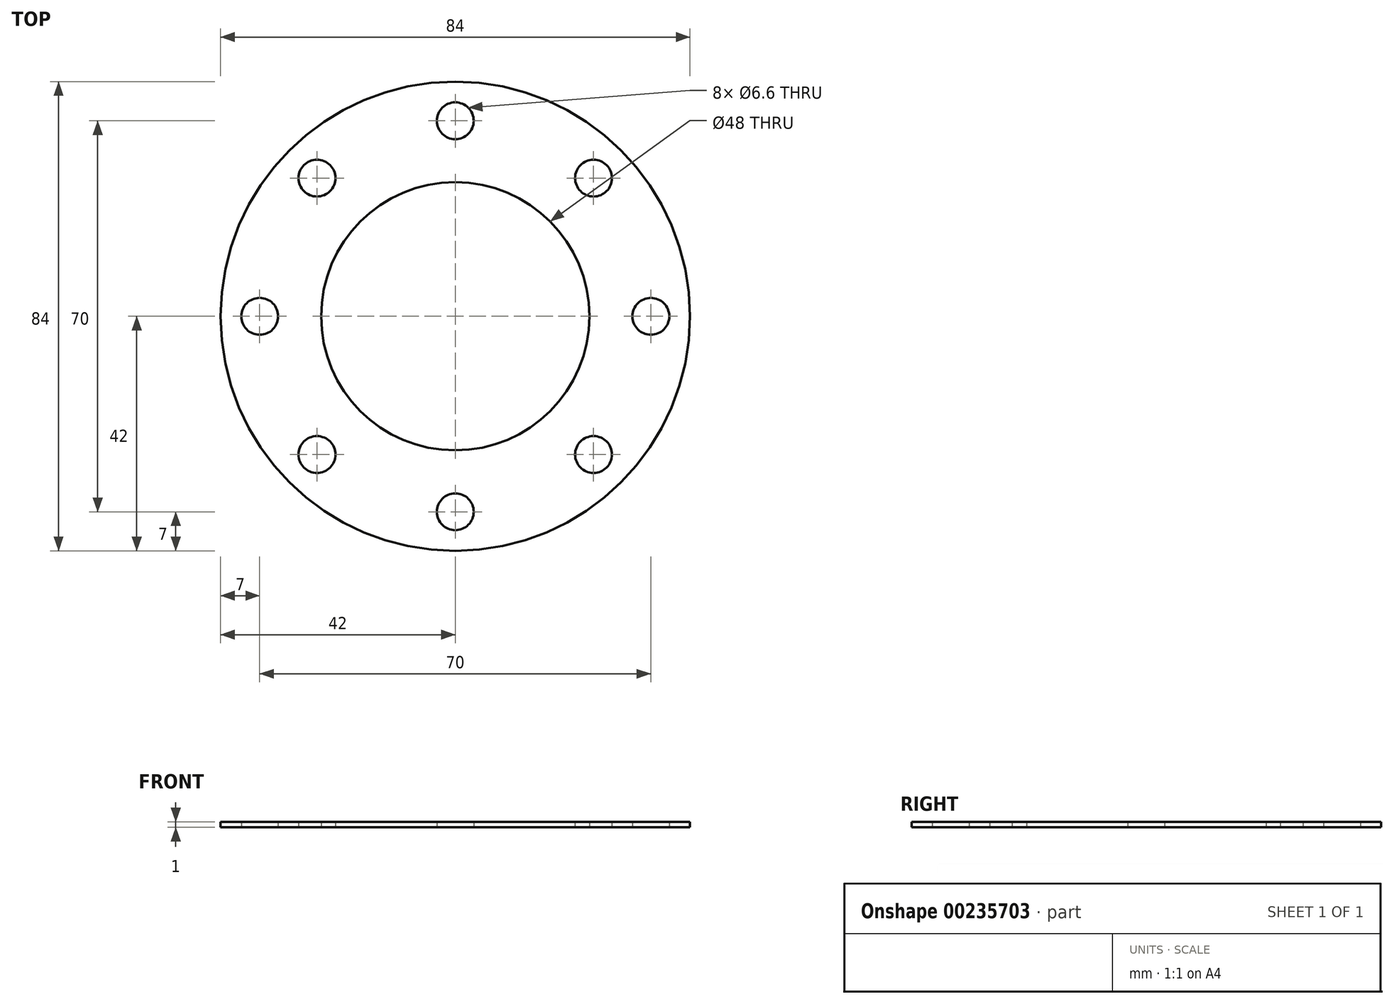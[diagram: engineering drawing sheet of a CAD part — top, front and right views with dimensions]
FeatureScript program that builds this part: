
annotation { "Feature Type Name" : "Feature", "Feature Type Description" : "" }
export const myFeature = defineFeature(function(context is Context, id is Id, definition is map)
    precondition{}
    {
        {
            var Q0;
            Q0=qCreatedBy(makeId("Top.planeOp"),FACE);
            var sketch = newSketch(context, id + "F0", { "sketchPlane" : qUnion([Q0])});
            skCircle(sketch, "E0", {"center": v(0, 0) * mm, "radius": 42 * mm});
            skCircle(sketch, "E1", {"center": v(0, 0) * mm, "radius": 24 * mm});
            skLineSegment(sketch, "E2", {"start": v(0, 0) * mm, "end": v(0, 35) * mm, "construction": true});
            skCircle(sketch, "E3", {"center": v(0, 0) * mm, "radius": 35 * mm, "construction": true});
            skLineSegment(sketch, "E4", {"start": v(0, 0) * mm, "end": v(0, -35) * mm, "construction": true});
            skLineSegment(sketch, "E5", {"start": v(0, 0) * mm, "end": v(35, 0) * mm, "construction": true});
            skLineSegment(sketch, "E6", {"start": v(0, 0) * mm, "end": v(-35, 0) * mm, "construction": true});
            skLineSegment(sketch, "E7", {"start": v(0, 0) * mm, "end": v(24.75, -24.75) * mm, "construction": true});
            skLineSegment(sketch, "E8", {"start": v(0, 0) * mm, "end": v(-24.75, -24.75) * mm, "construction": true});
            skLineSegment(sketch, "E9", {"start": v(0, 0) * mm, "end": v(-24.75, 24.75) * mm, "construction": true});
            skLineSegment(sketch, "E10", {"start": v(0, 0) * mm, "end": v(24.75, 24.75) * mm, "construction": true});
            skPoint(sketch, "E11.orphan", {"position": v(0, 42) * mm});
            skSolve(sketch);
        }
        {
            var Q0;
            Q0=makeQuery(id+"F0.imprint","IMPRINT",FACE,{"disambiguationData":[TD([[makeQuery(id+"F0.imprint","IMPRINT",EDGE,{"derivedFrom":sQuery(id+"F0.wireOp",EDGE,"E0")}),1.0]])]});
            var Q1;
            {var subQ0=sQuery(id+"F0.wireOp",EDGE,"8358ee84-de08-4119-9a5a-cfbe7e3d5f32.7.0");var subQ1=sQuery(id+"F0.wireOp",EDGE,"E1");var subQ2=makeQuery(id+"F0.imprint","INTERSECT",VERTEX,{"derivedFrom":[subQ1,subQ0]});Q1=makeQuery(id+"F0.imprint","IMPRINT",FACE,{"disambiguationData":[TD([[makeQuery(id+"F0.imprint","IMPRINT",EDGE,{"disambiguationData":[TD([[subQ2,1.0]])],"derivedFrom":subQ1}),-1.0]])]});}
            var Q2;
            {var subQ0=sQuery(id+"F0.wireOp",EDGE,"8358ee84-de08-4119-9a5a-cfbe7e3d5f32.7.0");var subQ1=sQuery(id+"F0.wireOp",EDGE,"E1");var subQ2=makeQuery(id+"F0.imprint","INTERSECT",VERTEX,{"derivedFrom":[subQ1,subQ0]});Q2=makeQuery(id+"F0.imprint","IMPRINT",FACE,{"disambiguationData":[TD([[makeQuery(id+"F0.imprint","IMPRINT",EDGE,{"disambiguationData":[TD([[subQ2,-1.0]])],"derivedFrom":subQ1}),-1.0]])]});}
            var Q3;
            {var subQ0=sQuery(id+"F0.wireOp",EDGE,"E2");var subQ1=sQuery(id+"F0.wireOp",EDGE,"E1");var subQ2=makeQuery(id+"F0.imprint","INTERSECT",VERTEX,{"derivedFrom":[subQ1,subQ0]});Q3=makeQuery(id+"F0.imprint","IMPRINT",FACE,{"disambiguationData":[TD([[makeQuery(id+"F0.imprint","IMPRINT",EDGE,{"disambiguationData":[TD([[subQ2,-1.0]])],"derivedFrom":subQ1}),-1.0]])]});}
            var Q4;
            {var subQ0=sQuery(id+"F0.wireOp",EDGE,"8358ee84-de08-4119-9a5a-cfbe7e3d5f32.4.0");var subQ1=sQuery(id+"F0.wireOp",EDGE,"E1");var subQ2=makeQuery(id+"F0.imprint","INTERSECT",VERTEX,{"derivedFrom":[subQ1,subQ0]});Q4=makeQuery(id+"F0.imprint","IMPRINT",FACE,{"disambiguationData":[TD([[makeQuery(id+"F0.imprint","IMPRINT",EDGE,{"disambiguationData":[TD([[subQ2,-1.0]])],"derivedFrom":subQ1}),-1.0]])]});}
            var Q5;
            {var subQ0=sQuery(id+"F0.wireOp",EDGE,"8358ee84-de08-4119-9a5a-cfbe7e3d5f32.6.0");var subQ1=sQuery(id+"F0.wireOp",EDGE,"E1");var subQ2=makeQuery(id+"F0.imprint","INTERSECT",VERTEX,{"derivedFrom":[subQ1,subQ0]});Q5=makeQuery(id+"F0.imprint","IMPRINT",FACE,{"disambiguationData":[TD([[makeQuery(id+"F0.imprint","IMPRINT",EDGE,{"disambiguationData":[TD([[subQ2,1.0]])],"derivedFrom":subQ1}),-1.0]])]});}
            var Q6;
            {var subQ0=sQuery(id+"F0.wireOp",EDGE,"8358ee84-de08-4119-9a5a-cfbe7e3d5f32.3.0");var subQ1=sQuery(id+"F0.wireOp",EDGE,"E1");var subQ2=makeQuery(id+"F0.imprint","INTERSECT",VERTEX,{"derivedFrom":[subQ1,subQ0]});Q6=makeQuery(id+"F0.imprint","IMPRINT",FACE,{"disambiguationData":[TD([[makeQuery(id+"F0.imprint","IMPRINT",EDGE,{"disambiguationData":[TD([[subQ2,-1.0]])],"derivedFrom":subQ1}),-1.0]])]});}
            var Q7;
            {var subQ0=sQuery(id+"F0.wireOp",EDGE,"8358ee84-de08-4119-9a5a-cfbe7e3d5f32.2.0");var subQ1=sQuery(id+"F0.wireOp",EDGE,"E1");var subQ2=makeQuery(id+"F0.imprint","INTERSECT",VERTEX,{"derivedFrom":[subQ1,subQ0]});Q7=makeQuery(id+"F0.imprint","IMPRINT",FACE,{"disambiguationData":[TD([[makeQuery(id+"F0.imprint","IMPRINT",EDGE,{"disambiguationData":[TD([[subQ2,-1.0]])],"derivedFrom":subQ1}),-1.0]])]});}
            var Q8;
            {var subQ0=sQuery(id+"F0.wireOp",EDGE,"8358ee84-de08-4119-9a5a-cfbe7e3d5f32.1.0");var subQ1=sQuery(id+"F0.wireOp",EDGE,"E1");var subQ2=makeQuery(id+"F0.imprint","INTERSECT",VERTEX,{"derivedFrom":[subQ1,subQ0]});Q8=makeQuery(id+"F0.imprint","IMPRINT",FACE,{"disambiguationData":[TD([[makeQuery(id+"F0.imprint","IMPRINT",EDGE,{"disambiguationData":[TD([[subQ2,-1.0]])],"derivedFrom":subQ1}),-1.0]])]});}
            extrude(context, id + "F1", {"entities" : qUnion([Q0, Q1, Q2, Q3, Q4, Q5, Q6, Q7, Q8]), "depth" : 1 * mm});
        }
        {
            var Q0;
            Q0=sQuery(id+"F0.wireOp",VERTEX,"E8.end");
            var Q1;
            Q1=sQuery(id+"F0.wireOp",VERTEX,"E4.end");
            var Q2;
            Q2=sQuery(id+"F0.wireOp",VERTEX,"E7.end");
            var Q3;
            Q3=sQuery(id+"F0.wireOp",VERTEX,"E5.end");
            var Q4;
            Q4=sQuery(id+"F0.wireOp",VERTEX,"E10.end");
            var Q5;
            Q5=sQuery(id+"F0.wireOp",VERTEX,"E2.end");
            var Q6;
            Q6=sQuery(id+"F0.wireOp",VERTEX,"E9.end");
            var Q7;
            Q7=sQuery(id+"F0.wireOp",VERTEX,"E6.end");
            var Q8;
            Q8=makeQuery(id+"F1.opExtrude","SWEPT_BODY",BODY,{"disambiguationData":[OSD([sQuery(id+"F0.wireOp",EDGE,"E0"),sQuery(id+"F0.wireOp",EDGE,"E1")])]});
            hole(context, id + "F2", {"style" : HoleStyle.SIMPLE, "endStyle" : HoleEndStyle.BLIND, "oppositeDirection" : true, "standardTappedOrClearance" : lookupTablePath({ "standard" : "ISO", "fit" : "Normal", "size" : "M6", "type" : "Clearance" }), "standardBlindInLast" : lookupTablePath({ "fit" : "Standard", "standard" : "ISO", "size" : "M6", "type" : "Clearance" }), "holeDiameter" : 6.6 * mm, "holeDepth" : 12 * mm, "tappedDepth" : 9 * mm, "tapClearance" : 3, "startFromSketch" : true, "locations" : qUnion([Q0, Q1, Q2, Q3, Q4, Q5, Q6, Q7]), "scope" : qUnion([Q8])});
        }
    });
